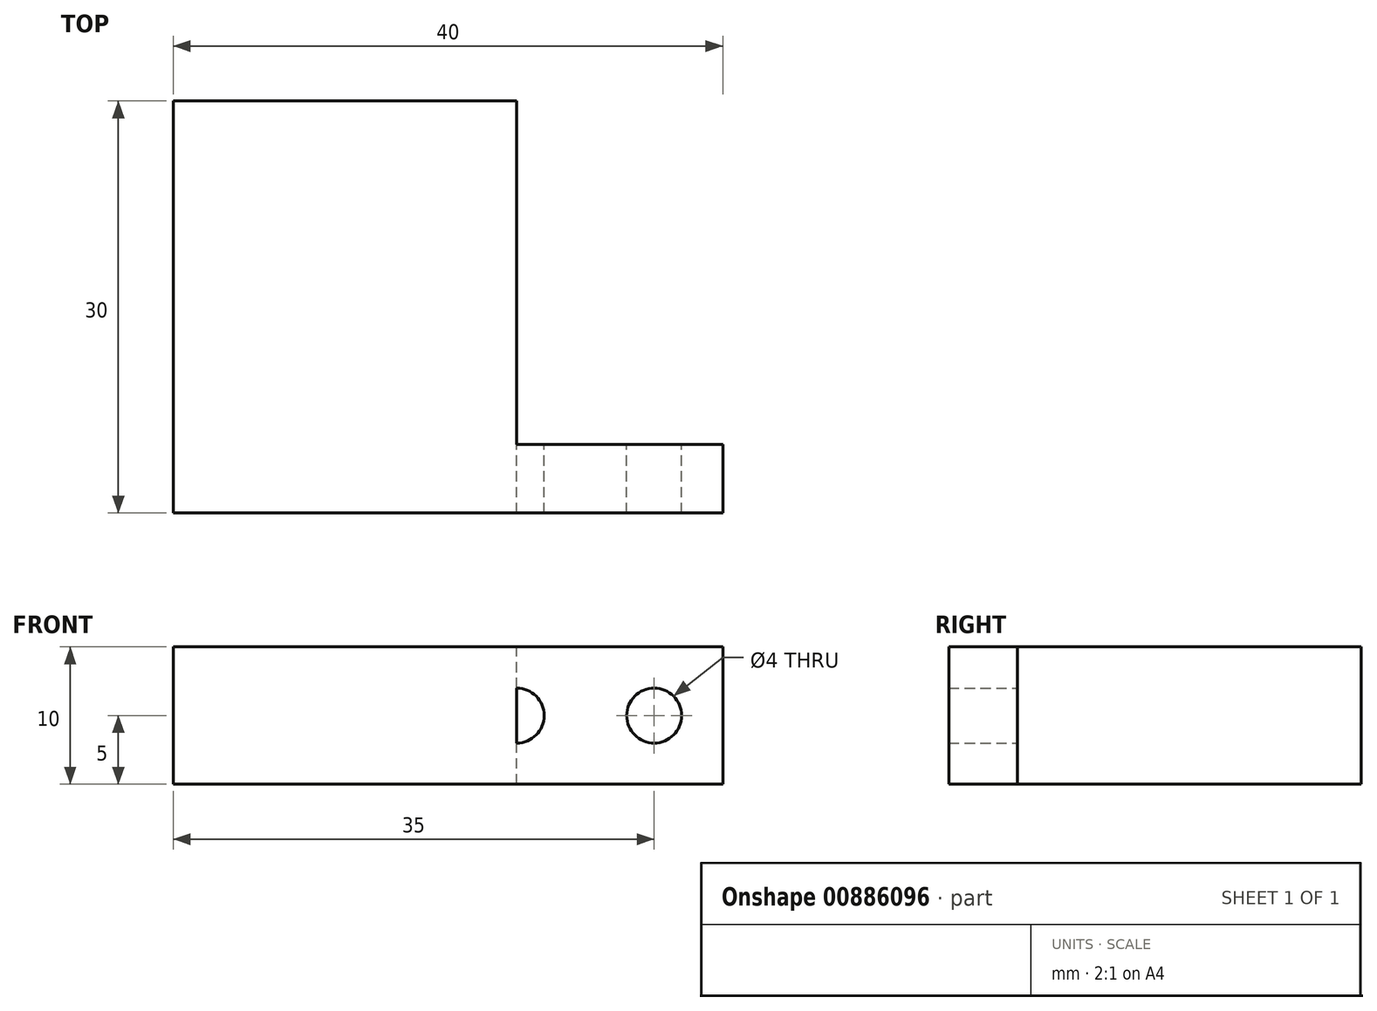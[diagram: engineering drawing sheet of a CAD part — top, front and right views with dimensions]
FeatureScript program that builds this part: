
annotation { "Feature Type Name" : "Feature", "Feature Type Description" : "" }
export const myFeature = defineFeature(function(context is Context, id is Id, definition is map)
    precondition{}
    {
        {
            var Q0;
            Q0=qCreatedBy(makeId("Front.planeOp"),FACE);
            var sketch = newSketch(context, id + "F0", { "sketchPlane" : qUnion([Q0])});
            skLineSegment(sketch, "E0.bottom", {"start": v(-20, 5) * mm, "end": v(20, 5) * mm});
            skLineSegment(sketch, "E0.top", {"start": v(-20, -5) * mm, "end": v(20, -5) * mm});
            skLineSegment(sketch, "E0.left", {"start": v(-20, 5) * mm, "end": v(-20, -5) * mm});
            skLineSegment(sketch, "E0.right", {"start": v(20, 5) * mm, "end": v(20, -5) * mm});
            skPoint(sketch, "E0.middle", {"position": v(0, 0) * mm});
            skCircle(sketch, "E1", {"center": v(15, 0) * mm, "radius": 2 * mm});
            skCircle(sketch, "E2", {"center": v(5, 0) * mm, "radius": 2 * mm});
            skSolve(sketch);
        }
        {
            var Q0;
            Q0 = qSketchRegion(id + "F0", true);
            extrude(context, id + "F1", {"entities" : qUnion([Q0]), "depth" : 5 * mm, "offsetDistance" : 25 * mm});
        }
        {
            var Q0;
            Q0=makeQuery(id+"F1.opExtrude","SWEPT_FACE",FACE,{"disambiguationData":[OSD([sQuery(id+"F0.wireOp",EDGE,"E0.bottom")])]});
            var sketch = newSketch(context, id + "F2", { "sketchPlane" : qUnion([Q0])});
            skLineSegment(sketch, "E3.bottom", {"start": v(-20, -5) * mm, "end": v(5, -5) * mm});
            skLineSegment(sketch, "E3.top", {"start": v(-20, 25) * mm, "end": v(5, 25) * mm});
            skLineSegment(sketch, "E3.left", {"start": v(-20, -5) * mm, "end": v(-20, 25) * mm});
            skLineSegment(sketch, "E3.right", {"start": v(5, -5) * mm, "end": v(5, 25) * mm});
            skSolve(sketch);
        }
        {
            var Q0;
            Q0 = qSketchRegion(id + "F2", true);
            extrude(context, id + "F3", {"entities" : qUnion([Q0]), "operationType" : NewBodyOperationType.ADD, "oppositeDirection" : true, "depth" : 10 * mm, "offsetDistance" : 25 * mm});
        }
    });
